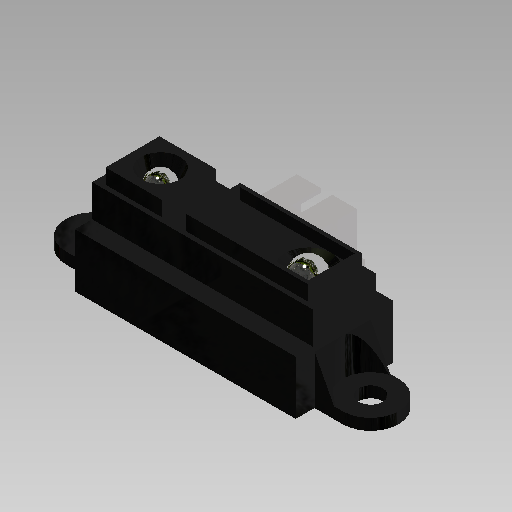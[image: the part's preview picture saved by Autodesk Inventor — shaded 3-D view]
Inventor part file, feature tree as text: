
AUTODESK INVENTOR PART (.ipt)
format: ipt  version: 2020 (Build 240168000, 168)  size: 441,344 bytes
history: native  units: mm
features: sketch x27, extrude x17, plane x3, mirror x3, revolve x3, loft x2, projected_geometry x2
ambient origin geometry x8: Origin, YZ Plane, XZ Plane, XY Plane, X Axis, Y Axis, Z Axis, Center Point
bodies: Solid1 (feature_tree)
feature tree (57):
  extrude  "Extrusion1"  Depth=13.0mm
  extrude  "Extrusion2"  Depth=4.2mm
  extrude  "Extrusion3"  Depth=6.3mm TaperAngle=0.0deg
  extrude  "Extrusion4"  Depth=7.2mm
  extrude  "Extrusion5"  Depth=1.2mm
  extrude  "Extrusion6"  Depth=2.0mm TaperAngle=0.0deg
  extrude  "Extrusion7"  Depth=7.5mm
  sketch  "Sketch8"  dims[d18=2.0mm d19=0.0mm d20=6.3mm d21=0.0mm]
  sketch  "Sketch9"  dims[d22=3.75mm d23=3.2mm]
  plane  "Work Plane1"
  extrude  "Extrusion8"  Depth=6.3mm TaperAngle=0.0deg
  extrude  "Extrusion9"  Depth=3.75mm
  plane  "Work Plane2"
  mirror  "Mirror1"
  loft  "Loft1"
  sketch  "Sketch14"  dims[d36=0.0mm d37=90.0deg d38=90.0deg]
  plane  "Work Plane3"
  revolve  "Revolution1"  [1 undecoded]
  revolve  "Revolution2"  [1 undecoded]
  extrude  "Extrusion10"  TaperAngle=0.0deg  [1 undecoded]
  loft  "Loft2"
  extrude  "Extrusion11"  Depth=0.5mm
  revolve  "Revolution3"  [1 undecoded]
  extrude  "Extrusion12"  Depth=1.5mm TaperAngle=0.0deg
  extrude  "Extrusion13"  Depth=4.2mm
  mirror  "Mirror2"
  extrude  "Extrusion14"  TaperAngle=0.0deg  [1 undecoded]
  extrude  "Extrusion15"  TaperAngle=90.0deg  [1 undecoded]
  mirror  "Mirror3"
  extrude  "Extrusion16"  Depth=3.3mm
  extrude  "Extrusion17"  Depth=5.9mm TaperAngle=0.0deg
  sketch  "Sketch1"  dims[d0=29.5mm d1=13.0mm]
  sketch  "Sketch2"  dims[d2=13.5mm d3=0.0mm d4=4.2mm]
  sketch  "Sketch3"  dims[d5=8.4mm d6=6.3mm d7=0.0mm]
  sketch  "Sketch4"  dims[d8=3.6mm d9=7.2mm]
  sketch  "Sketch5"  dims[d10=2.0mm d11=0.0mm d12=1.2mm]
  sketch  "Sketch6"  dims[d13=1.2mm d14=2.0mm d15=0.0mm]
  sketch  "Sketch7"  dims[d16=16.3mm d17=7.5mm]
  sketch  "Sketch10"  dims[d24=1.5mm d25=0.0mm d26=2.6mm]
  sketch  "Sketch11"  dims[d27=5.0mm d28=1.5mm d29=0.0mm]
  sketch  "Sketch12"  dims[d30=1.5mm d31=0.0mm d32=1.0mm]
  sketch  "Sketch13"  dims[d33=3.5mm d34=0.0mm d35=90.0deg]
  sketch  "Sketch15"  dims[d39=90.0deg d40=0.5mm]
  sketch  "Sketch16"  dims[d41=0.5mm d42=0.5mm]
  sketch  "Sketch17"  dims[d43=0.5mm d44=1.5mm d45=0.0mm]
  sketch  "Sketch18"  dims[d46=6.2mm d47=4.2mm]
  projected_geometry  "Projected Loop1"
  sketch  "Sketch19"  dims[d48=0.0mm d49=90.0deg d50=0.0mm d51=90.0deg]
  sketch  "Sketch20"  dims[d52=0.5mm d53=0.0mm d54=90.0deg]
  sketch  "Sketch21"  dims[d55=3.3mm d56=5.05mm]
  projected_geometry  "Projected Loop2"
  sketch  "Sketch22"  dims[d57=10.1mm d58=5.9mm d59=0.0mm]
  sketch  "Sketch23"  dims[d60=4.0mm]
  sketch  "Sketch24"  dims[d61=5.3mm d62=0.0mm]
  sketch  "Sketch25"  dims[d65=0.5mm]
  sketch  "Sketch26"  dims[d66=0.5mm]
  sketch  "Sketch27"  dims[d67=4.5mm d68=0.0mm d69=2.0mm d70=0.7mm d71=0.5mm d72=0.0mm d73=0.75mm d74=4.0mm d75=1.5mm d76=0.5mm d77=0.0mm d78=45.0deg d79=0.5mm d80=0.5mm d81=3.3mm d82=0.0mm]
note: 6 required parameter values undecoded (feature->parameter linkage not recoverable at this tier; creation-order binding heuristic only, values carry confidence <= 0.55)